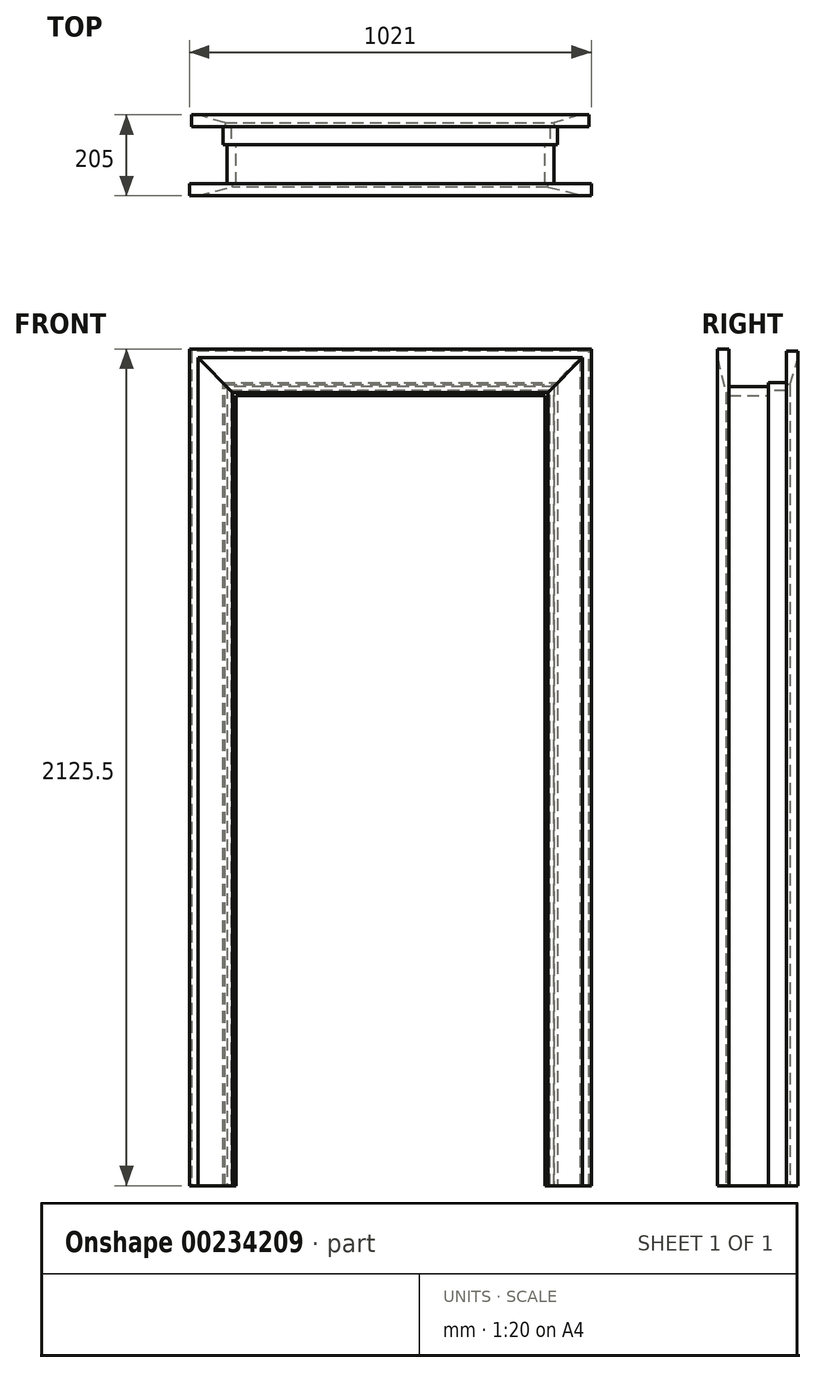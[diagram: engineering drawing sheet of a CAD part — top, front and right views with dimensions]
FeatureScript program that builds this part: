
annotation { "Feature Type Name" : "Feature", "Feature Type Description" : "" }
export const myFeature = defineFeature(function(context is Context, id is Id, definition is map)
    precondition{}
    {
        {
            var Q0;
            Q0=qCreatedBy(makeId("Front.planeOp"),FACE);
            var sketch = newSketch(context, id + "F0", { "sketchPlane" : qUnion([Q0])});
            skLineSegment(sketch, "E0", {"start": v(0, 0) * mm, "end": v(0, 2007.5) * mm});
            skLineSegment(sketch, "E1", {"start": v(0, 2007.5) * mm, "end": v(785, 2007.5) * mm});
            skLineSegment(sketch, "E2", {"start": v(785, 2007.5) * mm, "end": v(785, 0) * mm});
            skLineSegment(sketch, "E3", {"start": v(785, 0) * mm, "end": v(807.5, 0) * mm});
            skLineSegment(sketch, "E4", {"start": v(807.5, 0) * mm, "end": v(807.5, 2030) * mm});
            skLineSegment(sketch, "E5", {"start": v(807.5, 2030) * mm, "end": v(-22.5, 2030) * mm});
            skLineSegment(sketch, "E6", {"start": v(-22.5, 2030) * mm, "end": v(-22.5, 0) * mm});
            skLineSegment(sketch, "E7", {"start": v(-22.5, 0) * mm, "end": v(0, 0) * mm});
            skSolve(sketch);
        }
        {
            var Q0;
            Q0=makeQuery(id+"F0.imprint","IMPRINT",FACE,{"disambiguationData":[TD([[makeQuery(id+"F0.imprint","IMPRINT",EDGE,{"derivedFrom":sQuery(id+"F0.wireOp",EDGE,"E0")}),1.0]])]});
            extrude(context, id + "F1", {"entities" : qUnion([Q0]), "depth" : 100 * mm});
        }
        {
            var Q0;
            Q0=makeQuery(id+"F1.opExtrude","CAP_FACE",FACE,{"disambiguationData":[OSD([sQuery(id+"F0.wireOp",EDGE,"E0"),sQuery(id+"F0.wireOp",EDGE,"E1"),sQuery(id+"F0.wireOp",EDGE,"E2"),sQuery(id+"F0.wireOp",EDGE,"E3"),sQuery(id+"F0.wireOp",EDGE,"E4"),sQuery(id+"F0.wireOp",EDGE,"E5"),sQuery(id+"F0.wireOp",EDGE,"E6"),sQuery(id+"F0.wireOp",EDGE,"E7")])],"isStart":true});
            var sketch = newSketch(context, id + "F2", { "sketchPlane" : qUnion([Q0])});
            skLineSegment(sketch, "E8", {"start": v(22.5, 0) * mm, "end": v(32.5, 0) * mm});
            skLineSegment(sketch, "E9", {"start": v(32.5, 0) * mm, "end": v(32.5, 2040) * mm});
            skLineSegment(sketch, "E10", {"start": v(32.5, 2040) * mm, "end": v(-817.5, 2040) * mm});
            skLineSegment(sketch, "E11", {"start": v(-817.5, 2040) * mm, "end": v(-817.5, 0) * mm});
            skLineSegment(sketch, "E12", {"start": v(-817.5, 0) * mm, "end": v(-807.5, 0) * mm});
            skLineSegment(sketch, "E13", {"start": v(-807.5, 0) * mm, "end": v(-807.5, 2030) * mm, "construction": true});
            skLineSegment(sketch, "E14", {"start": v(-807.5, 2030) * mm, "end": v(22.5, 2030) * mm, "construction": true});
            skLineSegment(sketch, "E15", {"start": v(22.5, 2030) * mm, "end": v(22.5, 0) * mm, "construction": true});
            skLineSegment(sketch, "E16", {"start": v(-807.5, 0) * mm, "end": v(-797.5, 0) * mm});
            skLineSegment(sketch, "E17", {"start": v(-797.5, 0) * mm, "end": v(-797.5, 2020) * mm});
            skLineSegment(sketch, "E18", {"start": v(-797.5, 2020) * mm, "end": v(12.5, 2020) * mm});
            skLineSegment(sketch, "E19", {"start": v(12.5, 2020) * mm, "end": v(12.5, 0) * mm});
            skLineSegment(sketch, "E20", {"start": v(12.5, 0) * mm, "end": v(22.5, 0) * mm});
            skSolve(sketch);
        }
        {
            var Q0;
            Q0=qSketchRegion(id+"F2",true);
            extrude(context, id + "F3", {"entities" : qUnion([Q0]), "operationType" : NewBodyOperationType.ADD, "depth" : 45 * mm});
        }
        {
            var Q0;
            Q0=makeQuery(id+"F3.opExtrude","CAP_FACE",FACE,{"disambiguationData":[OSD([sQuery(id+"F2.wireOp",EDGE,"E8"),sQuery(id+"F2.wireOp",EDGE,"E9"),sQuery(id+"F2.wireOp",EDGE,"E10"),sQuery(id+"F2.wireOp",EDGE,"E11"),sQuery(id+"F2.wireOp",EDGE,"E12"),sQuery(id+"F2.wireOp",EDGE,"E13"),sQuery(id+"F2.wireOp",EDGE,"E14"),sQuery(id+"F2.wireOp",EDGE,"E15")])],"isStart":false});
            var sketch = newSketch(context, id + "F4", { "sketchPlane" : qUnion([Q0])});
            skLineSegment(sketch, "E21", {"start": v(32.5, 2040) * mm, "end": v(-817.5, 2040) * mm, "construction": true});
            skLineSegment(sketch, "E22", {"start": v(-817.5, 2040) * mm, "end": v(-817.5, 0) * mm, "construction": true});
            skLineSegment(sketch, "E23", {"start": v(-817.5, 0) * mm, "end": v(-897.5, 0) * mm});
            skLineSegment(sketch, "E24", {"start": v(-897.5, 0) * mm, "end": v(-897.5, 2120) * mm});
            skLineSegment(sketch, "E25", {"start": v(-897.5, 2120) * mm, "end": v(112.5, 2120) * mm});
            skLineSegment(sketch, "E26", {"start": v(112.5, 2120) * mm, "end": v(112.5, 0) * mm});
            skLineSegment(sketch, "E27", {"start": v(112.5, 0) * mm, "end": v(32.5, 0) * mm});
            skLineSegment(sketch, "E28", {"start": v(32.5, 0) * mm, "end": v(32.5, 2040) * mm, "construction": true});
            skLineSegment(sketch, "E29", {"start": v(32.5, 0) * mm, "end": v(27.5, 0) * mm});
            skLineSegment(sketch, "E30", {"start": v(27.5, 0) * mm, "end": v(27.5, 2035) * mm});
            skLineSegment(sketch, "E31", {"start": v(27.5, 2035) * mm, "end": v(-807.5, 2035) * mm});
            skLineSegment(sketch, "E32", {"start": v(-807.5, 2035) * mm, "end": v(-807.5, 0) * mm});
            skPoint(sketch, "E32.endSnap0", {"position": v(-807.5, 0) * mm});
            skLineSegment(sketch, "E33", {"start": v(-807.5, 0) * mm, "end": v(-817.5, 0) * mm});
            skSolve(sketch);
        }
        {
            var Q0;
            Q0=qSketchRegion(id+"F4",true);
            extrude(context, id + "F5", {"entities" : qUnion([Q0]), "operationType" : NewBodyOperationType.ADD, "depth" : 30 * mm});
        }
        {
            var Q0;
            Q0=makeQuery(id+"F5.opExtrude","CAP_EDGE",EDGE,{"disambiguationData":[OSD([sQuery(id+"F4.wireOp",EDGE,"E31")])],"isStart":false});
            var Q1;
            Q1=makeQuery(id+"F5.opExtrude","CAP_EDGE",EDGE,{"disambiguationData":[OSD([sQuery(id+"F4.wireOp",EDGE,"E30")])],"isStart":false});
            var Q2;
            Q2=makeQuery(id+"F5.opExtrude","CAP_EDGE",EDGE,{"disambiguationData":[OSD([sQuery(id+"F4.wireOp",EDGE,"E32")])],"isStart":false});
            chamfer(context, id + "F6", {"entities" : qUnion([Q0, Q1, Q2]), "chamferType" : ChamferType.TWO_OFFSETS, "width1" : 20 * mm, "oppositeDirection" : false, "width2" : 68 * mm, "tangentPropagation" : true});
        }
        {
            var Q0;
            Q0=makeQuery(id+"F1.opExtrude","CAP_FACE",FACE,{"disambiguationData":[OSD([sQuery(id+"F0.wireOp",EDGE,"E0"),sQuery(id+"F0.wireOp",EDGE,"E1"),sQuery(id+"F0.wireOp",EDGE,"E2"),sQuery(id+"F0.wireOp",EDGE,"E3"),sQuery(id+"F0.wireOp",EDGE,"E4"),sQuery(id+"F0.wireOp",EDGE,"E5"),sQuery(id+"F0.wireOp",EDGE,"E6"),sQuery(id+"F0.wireOp",EDGE,"E7")])],"isStart":false});
            var sketch = newSketch(context, id + "F7", { "sketchPlane" : qUnion([Q0])});
            skLineSegment(sketch, "E34", {"start": v(-8, 0) * mm, "end": v(-118, 0) * mm});
            skPoint(sketch, "E34.endSnap0", {"position": v(-11.25, 0) * mm});
            skLineSegment(sketch, "E35", {"start": v(-118, 0) * mm, "end": v(-118, 2125.5) * mm});
            skLineSegment(sketch, "E36", {"start": v(-118, 2125.5) * mm, "end": v(903, 2125.5) * mm});
            skLineSegment(sketch, "E37", {"start": v(903, 2125.5) * mm, "end": v(903, 0) * mm});
            skLineSegment(sketch, "E38", {"start": v(903, 0) * mm, "end": v(793, 0) * mm});
            skLineSegment(sketch, "E39", {"start": v(793, 0) * mm, "end": v(793, 2015.5) * mm});
            skLineSegment(sketch, "E40", {"start": v(793, 2015.5) * mm, "end": v(-8, 2015.5) * mm});
            skLineSegment(sketch, "E41", {"start": v(-8, 2015.5) * mm, "end": v(-8, 0) * mm});
            skSolve(sketch);
        }
        {
            var Q0;
            Q0=qSketchRegion(id+"F7",true);
            extrude(context, id + "F8", {"entities" : qUnion([Q0]), "operationType" : NewBodyOperationType.ADD, "depth" : 30 * mm});
        }
        {
            var Q0;
            Q0=makeQuery(id+"F8.opExtrude","CAP_EDGE",EDGE,{"disambiguationData":[OSD([sQuery(id+"F7.wireOp",EDGE,"E39")])],"isStart":false});
            var Q1;
            Q1=makeQuery(id+"F8.opExtrude","CAP_EDGE",EDGE,{"disambiguationData":[OSD([sQuery(id+"F7.wireOp",EDGE,"E40")])],"isStart":false});
            var Q2;
            Q2=makeQuery(id+"F8.opExtrude","CAP_EDGE",EDGE,{"disambiguationData":[OSD([sQuery(id+"F7.wireOp",EDGE,"E41")])],"isStart":false});
            chamfer(context, id + "F9", {"entities" : qUnion([Q0, Q1, Q2]), "chamferType" : ChamferType.TWO_OFFSETS, "width1" : 22 * mm, "oppositeDirection" : false, "width2" : 88 * mm, "tangentPropagation" : true});
        }
    });
